# Revit family: DOLED
name_source: partatom
category: Luminaires
units: mm (PartAtom-declared; Revit-internal decimal feet)

## family parameters
Cote de connecteur circulaire = Utiliser le diamètre
Couper avec des vides une fois chargée = Oui
Hôte = Face
Numéro OmniClass = 23.80.70.11.14.11
Partagée = Oui
Point de calcul de pièce = Oui
Source d'éclairage = Oui
Titre OmniClass = Downlights
Type d'élément = Normal

## types (11) — shared parameters
Angle de l'inclinaison = 60.00°
Emettre la visibilité des formes dans le rendu = Non
Emettre à partir du diamètre du cercle = 610 mm
Fabricant = Résistex
Filtre de couleur = 16777215
Garantie = 2 ans
Gradation des changements de température de couleur de lampe = <Aucun>
IK = 06
IP = 44
Image du type = <Aucun>
Indice de charge = Eclairage
Matériau collerette = PC Transparent
Modèle = Doled
Nombre pôles = 1
Tension = 230 V
URL = https://www.resistex-sa.com
Épaisseur = 45 mm  [stored 0.147638 ft]
Épaisseur collerette = 2 mm  [stored 0.00656168 ft]
zero-valued in all types: Elévation par défaut

## per-type parameters (varying)
| type | Charge apparente | Commentaires relatifs à la puissance | Coût | Description | Diamètre intérieur | Fichier de distribution photométrique | Rayon collerette | Rayon corps |
| 962411 | 13 VA | 12.1W | 32.5 $ | Downlight équipé d'une platine LED SMD, efficacité lumineuse de 119lm/W | 75 mm | 962411_LD.ies | 53 mm | 43 mm  [stored 0.141076 ft] |
| 962412 | 13 VA | 12.1W | 32.5 $ | Downlight équipé d'une platine LED SMD, efficacité lumineuse de 125lm/W | 75 mm | 962412.ies | 53 mm | 43 mm  [stored 0.141076 ft] |
| 962413 | 17 VA | 16.2W | 43 $ | Downlight équipé d'une platine LED SMD, efficacité lumineuse de 123lm/W | 143 mm | 962413.ies | 84 mm  [stored 0.275591 ft] | 78 mm |
| 962414 | 17 VA | 16.2W | 43 $ | Downlight équipé d'une platine LED SMD, efficacité lumineuse de 129lm/W | 143 mm | 962414.ies | 84 mm  [stored 0.275591 ft] | 78 mm |
| 962471 | 17 VA | 16.2W | 70 $ | Downlight équipé d'une platine LED SMD, efficacité lumineuse de 129lm/W | 143 mm | 962471.ies | 84 mm  [stored 0.275591 ft] | 78 mm |
| 962472 | 17 VA | 16.2W | 70 $ | Downlight équipé d'une platine LED SMD, efficacité lumineuse de 129lm/W | 143 mm | 962472.ies | 84 mm  [stored 0.275591 ft] | 78 mm |
| 962454 | 17 VA | 16.2W | 50 $ | Downlight équipé d'une platine LED SMD, efficacité lumineuse de 127lm/W | 182 mm | 962454.ies | 113 mm | 98 mm |
| 962453 | 17 VA | 16.2W | 50 $ | Downlight équipé d'une platine LED SMD, efficacité lumineuse de 123lm/W | 182 mm | 962453.ies | 113 mm | 98 mm |
| 962460 | 17 VA | 16.2W | 87.5 $ | Downlight équipé d'une platine LED SMD, efficacité lumineuse de 123lm/W | 182 mm | 962460.ies | 113 mm | 98 mm |
| 962457 | 17 VA | 16.2W | 87.5 $ | Downlight équipé d'une platine LED SMD, efficacité lumineuse de 127lm/W | 182 mm | 962457.ies | 113 mm | 98 mm |
| 962488 | 28 VA | 16.6W | 17.5 $ | Downlight équipé d'une platine LED SMD, efficacité lumineuse de 96.3lm/W | 138 mm | 962488.ies | 85 mm | 73 mm |

note: [stored X ft] marks values corroborated as IEEE doubles in the binary element streams (Revit-internal decimal feet)
